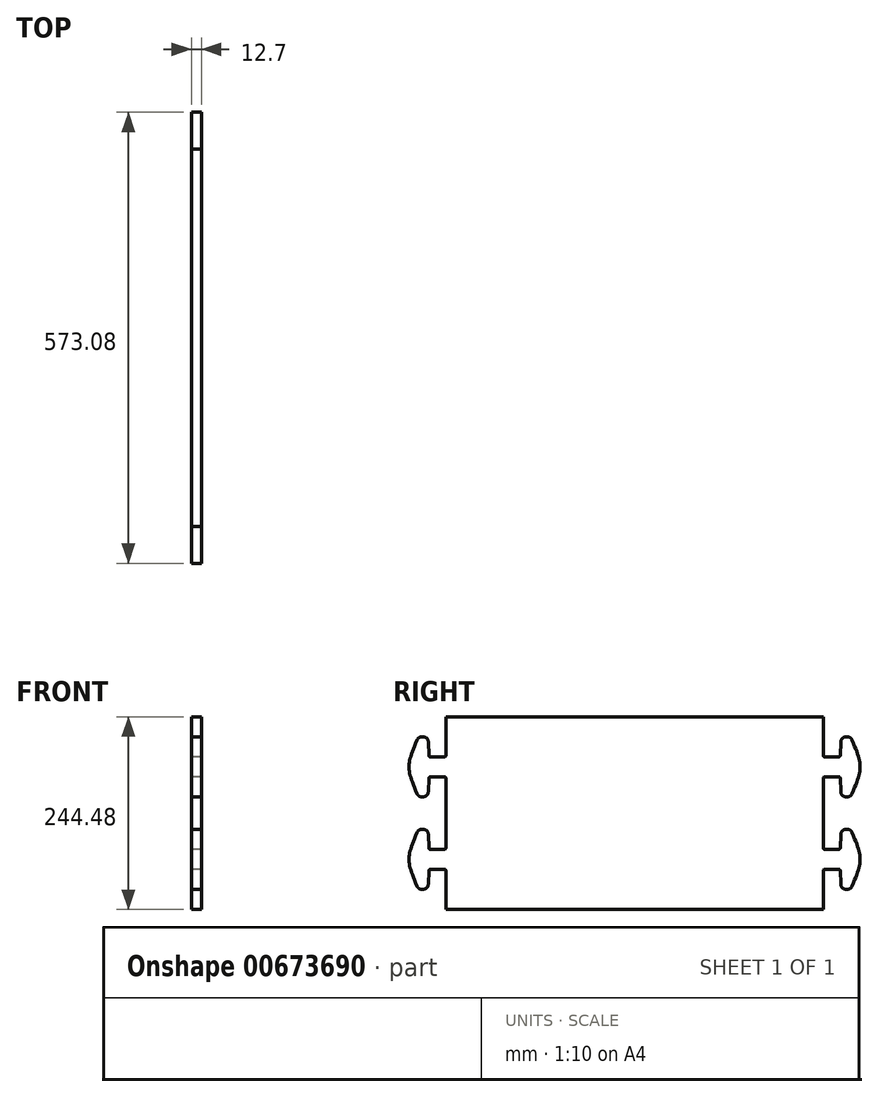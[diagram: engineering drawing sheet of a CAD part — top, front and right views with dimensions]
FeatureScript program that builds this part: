
annotation { "Feature Type Name" : "Feature", "Feature Type Description" : "" }
export const myFeature = defineFeature(function(context is Context, id is Id, definition is map)
    precondition{}
    {
        {
            var Q0;
            Q0=qCreatedBy(makeId("Right.planeOp"),FACE);
            var sketch = newSketch(context, id + "F0", { "sketchPlane" : qUnion([Q0])});
            skLineSegment(sketch, "E0", {"start": v(-281.1, 96.84) * mm, "end": v(-283.1, 96.84) * mm});
            skFitSpline(sketch, "E1", {"points": [v(-287.34, 96.84) * mm, v(-287.34, 20.64) * mm], "startDerivative": vector(-47.62, -114.3) * mm, "endDerivative": vector(47.62, -114.3) * mm});
            skLineSegment(sketch, "E2", {"start": v(-252.41, 58.74) * mm, "end": v(-303.21, 58.74) * mm, "construction": true});
            skLineSegment(sketch, "E3.MirrorCS", {"start": v(-274.75, 26.7) * mm, "end": v(-273.91, 44.52) * mm});
            skLineSegment(sketch, "E4.MirrorCS", {"start": v(-281.1, 20.64) * mm, "end": v(-283.1, 20.64) * mm});
            skLineSegment(sketch, "E5.MirrorCS", {"start": v(-274.75, 90.78) * mm, "end": v(-273.91, 72.95) * mm});
            skLineSegment(sketch, "E6.MirrorCS", {"start": v(-254, 46.04) * mm, "end": v(-272.33, 46.04) * mm});
            skLineSegment(sketch, "E7.MirrorCS", {"start": v(-272.33, 71.44) * mm, "end": v(-254, 71.44) * mm});
            skLineSegment(sketch, "E8.bottom", {"start": v(-252.41, -122.24) * mm, "end": v(227.01, -122.24) * mm});
            skLineSegment(sketch, "E8.top", {"start": v(-252.41, 122.24) * mm, "end": v(227.01, 122.24) * mm});
            skLineSegment(sketch, "E8.left", {"start": v(-252.41, 73.03) * mm, "end": v(-252.41, 122.24) * mm});
            skPoint(sketch, "E9.visualSharp", {"position": v(-275.03, 20.64) * mm});
            skArc(sketch, "E9.filletArc", {"start": v(-281.1, 20.64) * mm, "mid": v(-276.7, 22.4) * mm, "end": v(-274.75, 26.7) * mm});
            skPoint(sketch, "E10.visualSharp", {"position": v(-275.03, 96.84) * mm});
            skArc(sketch, "E10.filletArc", {"start": v(-274.75, 90.78) * mm, "mid": v(-276.7, 95.08) * mm, "end": v(-281.1, 96.84) * mm});
            skArc(sketch, "E11.filletArc", {"start": v(-283.1, 96.84) * mm, "mid": v(-286.63, 95.77) * mm, "end": v(-288.97, 92.92) * mm});
            skArc(sketch, "E12.filletArc", {"start": v(-288.97, 24.55) * mm, "mid": v(-286.63, 21.7) * mm, "end": v(-283.1, 20.64) * mm});
            skPoint(sketch, "E13.visualSharp", {"position": v(-273.84, 46.04) * mm});
            skArc(sketch, "E13.filletArc", {"start": v(-272.33, 46.04) * mm, "mid": v(-273.42, 45.6) * mm, "end": v(-273.91, 44.52) * mm});
            skPoint(sketch, "E14.visualSharp", {"position": v(-273.84, 71.44) * mm});
            skArc(sketch, "E14.filletArc", {"start": v(-273.91, 72.95) * mm, "mid": v(-273.42, 71.88) * mm, "end": v(-272.33, 71.44) * mm});
            skPoint(sketch, "E15.newPointB", {"position": v(-252.41, -122.24) * mm});
            skArc(sketch, "E15.filletArc", {"start": v(-254, 71.44) * mm, "mid": v(-252.88, 71.9) * mm, "end": v(-252.41, 73.03) * mm});
            skPoint(sketch, "E16.visualSharp", {"position": v(-252.41, 46.04) * mm});
            skArc(sketch, "E16.filletArc", {"start": v(-252.41, 44.45) * mm, "mid": v(-252.88, 45.57) * mm, "end": v(-254, 46.04) * mm});
            skArc(sketch, "E17.MirrorCS", {"start": v(-252.41, -44.45) * mm, "mid": v(-252.88, -45.57) * mm, "end": v(-254, -46.04) * mm});
            skLineSegment(sketch, "E18.MirrorCS", {"start": v(-254, -46.04) * mm, "end": v(-272.33, -46.04) * mm});
            skArc(sketch, "E19.MirrorCS", {"start": v(-254, -71.44) * mm, "mid": v(-252.88, -71.9) * mm, "end": v(-252.41, -73.03) * mm});
            skLineSegment(sketch, "E20.MirrorCS", {"start": v(-272.33, -71.44) * mm, "end": v(-254, -71.44) * mm});
            skArc(sketch, "E21.MirrorCS", {"start": v(-273.91, -72.95) * mm, "mid": v(-273.42, -71.88) * mm, "end": v(-272.33, -71.44) * mm});
            skLineSegment(sketch, "E22.MirrorCS", {"start": v(-274.75, -90.78) * mm, "end": v(-273.91, -72.95) * mm});
            skArc(sketch, "E23.MirrorCS", {"start": v(-274.75, -90.78) * mm, "mid": v(-276.7, -95.08) * mm, "end": v(-281.1, -96.84) * mm});
            skLineSegment(sketch, "E24.MirrorCS", {"start": v(-281.1, -96.84) * mm, "end": v(-283.1, -96.84) * mm});
            skArc(sketch, "E25.MirrorCS", {"start": v(-283.1, -96.84) * mm, "mid": v(-286.63, -95.77) * mm, "end": v(-288.97, -92.92) * mm});
            skFitSpline(sketch, "E26.MirrorCS", {"points": [v(-287.34, -96.84) * mm, v(-287.34, -20.64) * mm], "startDerivative": vector(-47.62, 114.3) * mm, "endDerivative": vector(47.62, 114.3) * mm});
            skArc(sketch, "E27.MirrorCS", {"start": v(-288.97, -24.55) * mm, "mid": v(-286.63, -21.7) * mm, "end": v(-283.1, -20.64) * mm});
            skLineSegment(sketch, "E28.MirrorCS", {"start": v(-281.1, -20.64) * mm, "end": v(-283.1, -20.64) * mm});
            skArc(sketch, "E29.MirrorCS", {"start": v(-281.1, -20.64) * mm, "mid": v(-276.7, -22.4) * mm, "end": v(-274.75, -26.7) * mm});
            skLineSegment(sketch, "E30.MirrorCS", {"start": v(-274.75, -26.7) * mm, "end": v(-273.91, -44.52) * mm});
            skArc(sketch, "E31.MirrorCS", {"start": v(-272.33, -46.04) * mm, "mid": v(-273.42, -45.6) * mm, "end": v(-273.91, -44.52) * mm});
            skLineSegment(sketch, "E32.MirrorCS", {"start": v(255.7, 96.84) * mm, "end": v(257.7, 96.84) * mm});
            skLineSegment(sketch, "E33.MirrorCS", {"start": v(255.7, 20.64) * mm, "end": v(257.7, 20.64) * mm});
            skArc(sketch, "E34.MirrorCS", {"start": v(248.51, 72.95) * mm, "mid": v(248.02, 71.88) * mm, "end": v(246.93, 71.44) * mm});
            skArc(sketch, "E35.MirrorCS", {"start": v(249.35, 90.78) * mm, "mid": v(251.3, 95.08) * mm, "end": v(255.7, 96.84) * mm});
            skLineSegment(sketch, "E36.MirrorCS", {"start": v(255.7, -96.84) * mm, "end": v(257.7, -96.84) * mm});
            skArc(sketch, "E37.MirrorCS", {"start": v(257.7, 96.84) * mm, "mid": v(261.23, 95.77) * mm, "end": v(263.57, 92.92) * mm});
            skArc(sketch, "E38.MirrorCS", {"start": v(255.7, 20.64) * mm, "mid": v(251.3, 22.4) * mm, "end": v(249.35, 26.7) * mm});
            skArc(sketch, "E39.MirrorCS", {"start": v(263.57, 24.55) * mm, "mid": v(261.23, 21.7) * mm, "end": v(257.7, 20.64) * mm});
            skArc(sketch, "E40.MirrorCS", {"start": v(228.6, 71.44) * mm, "mid": v(227.48, 71.9) * mm, "end": v(227.01, 73.03) * mm});
            skArc(sketch, "E41.MirrorCS", {"start": v(246.93, -46.04) * mm, "mid": v(248.02, -45.6) * mm, "end": v(248.51, -44.52) * mm});
            skArc(sketch, "E42.MirrorCS", {"start": v(227.01, 44.45) * mm, "mid": v(227.48, 45.57) * mm, "end": v(228.6, 46.04) * mm});
            skArc(sketch, "E43.MirrorCS", {"start": v(246.93, 46.04) * mm, "mid": v(248.02, 45.6) * mm, "end": v(248.51, 44.52) * mm});
            skArc(sketch, "E44.MirrorCS", {"start": v(255.7, -20.64) * mm, "mid": v(251.3, -22.4) * mm, "end": v(249.35, -26.7) * mm});
            skArc(sketch, "E45.MirrorCS", {"start": v(263.57, -24.55) * mm, "mid": v(261.23, -21.7) * mm, "end": v(257.7, -20.64) * mm});
            skArc(sketch, "E46.MirrorCS", {"start": v(227.01, -44.45) * mm, "mid": v(227.48, -45.57) * mm, "end": v(228.6, -46.04) * mm});
            skArc(sketch, "E47.MirrorCS", {"start": v(249.35, -90.78) * mm, "mid": v(251.3, -95.08) * mm, "end": v(255.7, -96.84) * mm});
            skArc(sketch, "E48.MirrorCS", {"start": v(257.7, -96.84) * mm, "mid": v(261.23, -95.77) * mm, "end": v(263.57, -92.92) * mm});
            skLineSegment(sketch, "E49.MirrorCS", {"start": v(249.35, 90.78) * mm, "end": v(248.51, 72.95) * mm});
            skLineSegment(sketch, "E50.MirrorCS", {"start": v(255.7, -20.64) * mm, "end": v(257.7, -20.64) * mm});
            skArc(sketch, "E51.MirrorCS", {"start": v(248.51, -72.95) * mm, "mid": v(248.02, -71.88) * mm, "end": v(246.93, -71.44) * mm});
            skLineSegment(sketch, "E52.MirrorCS", {"start": v(249.35, 26.7) * mm, "end": v(248.51, 44.52) * mm});
            skLineSegment(sketch, "E53.MirrorCS", {"start": v(249.35, -90.78) * mm, "end": v(248.51, -72.95) * mm});
            skArc(sketch, "E54.MirrorCS", {"start": v(228.6, -71.44) * mm, "mid": v(227.48, -71.9) * mm, "end": v(227.01, -73.03) * mm});
            skLineSegment(sketch, "E55.MirrorCS", {"start": v(228.6, 46.04) * mm, "end": v(246.93, 46.04) * mm});
            skLineSegment(sketch, "E56.MirrorCS", {"start": v(246.93, 71.44) * mm, "end": v(228.6, 71.44) * mm});
            skPoint(sketch, "E57.MirrorP", {"position": v(248.44, 46.04) * mm});
            skPoint(sketch, "E58.MirrorP", {"position": v(261.94, 96.84) * mm});
            skFitSpline(sketch, "E59.MirrorCS", {"points": [v(261.94, -96.84) * mm, v(261.94, -20.64) * mm], "startDerivative": vector(47.62, 114.3) * mm, "endDerivative": vector(-47.62, 114.3) * mm});
            skLineSegment(sketch, "E60.MirrorCS", {"start": v(227.01, 58.74) * mm, "end": v(277.81, 58.74) * mm, "construction": true});
            skLineSegment(sketch, "E61.MirrorCS", {"start": v(228.6, -46.04) * mm, "end": v(246.93, -46.04) * mm});
            skPoint(sketch, "E62.MirrorP", {"position": v(261.94, 20.64) * mm});
            skPoint(sketch, "E63.MirrorP", {"position": v(249.63, 20.64) * mm});
            skLineSegment(sketch, "E64.MirrorCS", {"start": v(249.35, -26.7) * mm, "end": v(248.51, -44.52) * mm});
            skLineSegment(sketch, "E65.MirrorCS", {"start": v(246.93, -71.44) * mm, "end": v(228.6, -71.44) * mm});
            skFitSpline(sketch, "E66.MirrorCS", {"points": [v(261.94, 96.84) * mm, v(261.94, 20.64) * mm], "startDerivative": vector(47.62, -114.3) * mm, "endDerivative": vector(-47.62, -114.3) * mm});
            skPoint(sketch, "E67.MirrorP", {"position": v(248.44, 71.44) * mm});
            skPoint(sketch, "E68.MirrorP", {"position": v(249.63, 96.84) * mm});
            skPoint(sketch, "E69.MirrorP", {"position": v(227.01, 46.04) * mm});
            skLineSegment(sketch, "E70", {"start": v(-252.41, 44.45) * mm, "end": v(-252.41, -44.45) * mm});
            skLineSegment(sketch, "E71", {"start": v(-252.41, -73.03) * mm, "end": v(-252.41, -122.24) * mm});
            skLineSegment(sketch, "E72", {"start": v(227.01, -122.24) * mm, "end": v(227.01, -73.03) * mm});
            skLineSegment(sketch, "E73", {"start": v(227.01, -44.45) * mm, "end": v(227.01, 44.45) * mm});
            skLineSegment(sketch, "E74", {"start": v(227.01, 73.03) * mm, "end": v(227.01, 122.24) * mm});
            skLineSegment(sketch, "E75", {"start": v(227.01, 0) * mm, "end": v(-252.41, 0) * mm, "construction": true});
            skLineSegment(sketch, "E76", {"start": v(-12.7, 122.24) * mm, "end": v(-12.7, -122.24) * mm, "construction": true});
            skSolve(sketch);
        }
        {
            var Q0;
            Q0=makeQuery(id+"F0.imprint","IMPRINT",FACE,{"disambiguationData":[TD([[makeQuery(id+"F0.imprint","IMPRINT",EDGE,{"derivedFrom":sQuery(id+"F0.wireOp",EDGE,"E0")}),1.0]])]});
            extrude(context, id + "F1", {"entities" : qUnion([Q0]), "depth" : 12.7 * mm, "offsetDistance" : 25.4 * mm});
        }
    });
